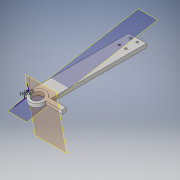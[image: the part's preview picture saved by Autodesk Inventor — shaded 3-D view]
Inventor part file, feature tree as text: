
AUTODESK INVENTOR PART (.ipt)
format: ipt  version: 2017 (Build 210142000, 142)  size: 164,352 bytes
history: native  units: in
note: dims shown in document units (in); Inventor stores cm internally (conversion verified against a paired STEP export)
features: sketch x6, projected_geometry x5, extrude x3, plane x2, hole x2
ambient origin geometry x8: Origin, YZ Plane, XZ Plane, XY Plane, X Axis, Y Axis, Z Axis, Center Point
bodies: Solid1 (feature_tree)
feature tree (18):
  extrude  "Extrusion1"  Depth=4.757in
  sketch  "Sketch2"  dims[d2=0.1875in d3=0.0in d4=0.6871in]
  plane  "Work Plane1"
  extrude  "Extrusion2"  Depth=0.1875in
  hole  "Hole2"  [1 undecoded]
  plane  "Work Plane3"
  hole  "Hole3"  [1 undecoded]
  extrude  "Extrusion4"  Depth=0.375in
  sketch  "Sketch1"  dims[d0=0.85in d1=4.757in]
  sketch  "Sketch3"  dims[d5=0.75in d6=0.85in]
  projected_geometry  "Projected Loop1"
  projected_geometry  "Projected Loop2"
  sketch  "Sketch5"  dims[d7=0.425in d8=0.1875in d9=0.0in]
  projected_geometry  "Projected Loop4"
  sketch  "Sketch9"  dims[d17=0.51in d18=0.75in d19=0.375in d20=0.25in d21=0.5635in d22=1.0in d23=0.8108in d24=0.0687in]
  projected_geometry  "Projected Loop10"
  sketch  "Sketch10"  dims[d25=90.0deg d34=0.6299in d35=0.315in d36=0.1575in d37=0.85in d38=0.425in d39=0.44in d40=0.11in d41=0.75in d42=0.375in d43=0.25in d44=0.5635in d45=1.0in d46=0.8108in d47=0.923in d48=0.1875in d49=0.0in]
  projected_geometry  "Projected Loop11"
note: 2 required parameter values undecoded (feature->parameter linkage not recoverable at this tier; creation-order binding heuristic only, values carry confidence <= 0.55)
